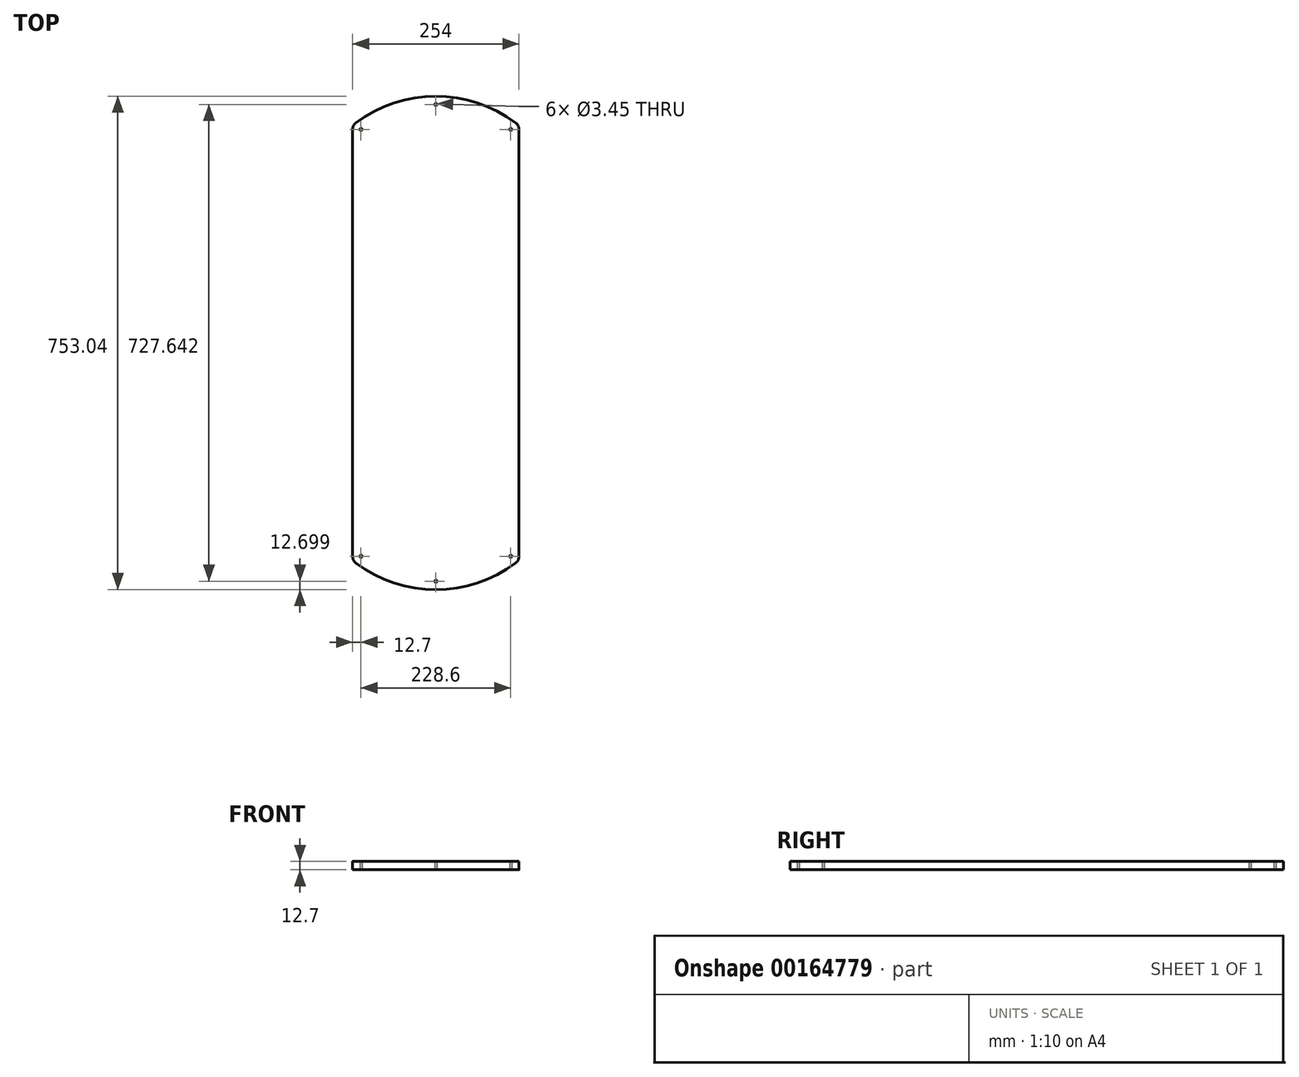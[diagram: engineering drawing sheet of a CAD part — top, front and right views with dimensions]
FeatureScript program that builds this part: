
annotation { "Feature Type Name" : "Feature", "Feature Type Description" : "" }
export const myFeature = defineFeature(function(context is Context, id is Id, definition is map)
    precondition{}
    {
        {
            var Q0;
            Q0=qCreatedBy(makeId("Top.planeOp"),FACE);
            var sketch = newSketch(context, id + "F0", { "sketchPlane" : qUnion([Q0])});
            skLineSegment(sketch, "E0.bottom", {"start": v(127, 325.72) * mm, "end": v(-127, 325.72) * mm, "construction": true});
            skLineSegment(sketch, "E0.top", {"start": v(127, -325.72) * mm, "end": v(-127, -325.72) * mm, "construction": true});
            skLineSegment(sketch, "E0.left", {"start": v(127, 325.72) * mm, "end": v(127, -325.72) * mm});
            skLineSegment(sketch, "E0.right", {"start": v(-127, 325.72) * mm, "end": v(-127, -325.72) * mm});
            skPoint(sketch, "E0.middle", {"position": v(0, 0) * mm});
            skArc(sketch, "E1", {"start": v(121.92, 335.88) * mm, "mid": v(0, 376.52) * mm, "end": v(-121.92, 335.88) * mm});
            skLineSegment(sketch, "E2", {"start": v(0, 325.72) * mm, "end": v(0, 173.32) * mm, "construction": true});
            skLineSegment(sketch, "E3", {"start": v(0, -173.32) * mm, "end": v(0, -325.72) * mm, "construction": true});
            skLineSegment(sketch, "E4", {"start": v(0, 173.32) * mm, "end": v(57.15, 249.52) * mm, "construction": true});
            skLineSegment(sketch, "E5", {"start": v(-57.15, 249.52) * mm, "end": v(0, 173.32) * mm, "construction": true});
            skLineSegment(sketch, "E6", {"start": v(0, 325.72) * mm, "end": v(0, 363.82) * mm, "construction": true});
            skCircle(sketch, "E7", {"center": v(0, 363.82) * mm, "radius": 12.7 * mm, "construction": true});
            skLineSegment(sketch, "E8", {"start": v(0, 249.52) * mm, "end": v(-57.15, 249.52) * mm, "construction": true});
            skLineSegment(sketch, "E9", {"start": v(0, 249.52) * mm, "end": v(57.15, 249.52) * mm, "construction": true});
            skLineSegment(sketch, "E10", {"start": v(-57.15, 249.52) * mm, "end": v(-114.3, 325.72) * mm, "construction": true});
            skLineSegment(sketch, "E11", {"start": v(57.15, 249.52) * mm, "end": v(114.3, 325.72) * mm, "construction": true});
            skCircle(sketch, "E12", {"center": v(-114.3, 325.72) * mm, "radius": 1.73 * mm});
            skCircle(sketch, "E13", {"center": v(114.3, 325.72) * mm, "radius": 1.73 * mm});
            skCircle(sketch, "E14", {"center": v(0, 363.82) * mm, "radius": 1.73 * mm});
            skArc(sketch, "E15", {"start": v(121.92, -335.88) * mm, "mid": v(125.66, -331.4) * mm, "end": v(127, -325.72) * mm});
            skArc(sketch, "E16", {"start": v(-127, -325.72) * mm, "mid": v(-125.66, -331.4) * mm, "end": v(-121.92, -335.88) * mm});
            skArc(sketch, "E17", {"start": v(-121.92, -335.88) * mm, "mid": v(0, -376.52) * mm, "end": v(121.92, -335.88) * mm});
            skArc(sketch, "E18", {"start": v(-121.92, 335.88) * mm, "mid": v(-125.66, 331.4) * mm, "end": v(-127, 325.72) * mm});
            skArc(sketch, "E19", {"start": v(127, 325.72) * mm, "mid": v(125.66, 331.4) * mm, "end": v(121.92, 335.88) * mm});
            skCircle(sketch, "E20", {"center": v(114.3, -325.72) * mm, "radius": 1.73 * mm});
            skCircle(sketch, "E21", {"center": v(-114.3, -325.72) * mm, "radius": 1.73 * mm});
            skLineSegment(sketch, "E22", {"start": v(0, -325.72) * mm, "end": v(0, -363.82) * mm, "construction": true});
            skCircle(sketch, "E23", {"center": v(0, -363.82) * mm, "radius": 12.7 * mm, "construction": true});
            skCircle(sketch, "E24", {"center": v(0, -363.82) * mm, "radius": 1.73 * mm});
            skSolve(sketch);
        }
        {
            var Q0;
            Q0=qSketchRegion(id+"F0",true);
            extrude(context, id + "F1", {"entities" : qUnion([Q0]), "depth" : 12.7 * mm});
        }
    });
